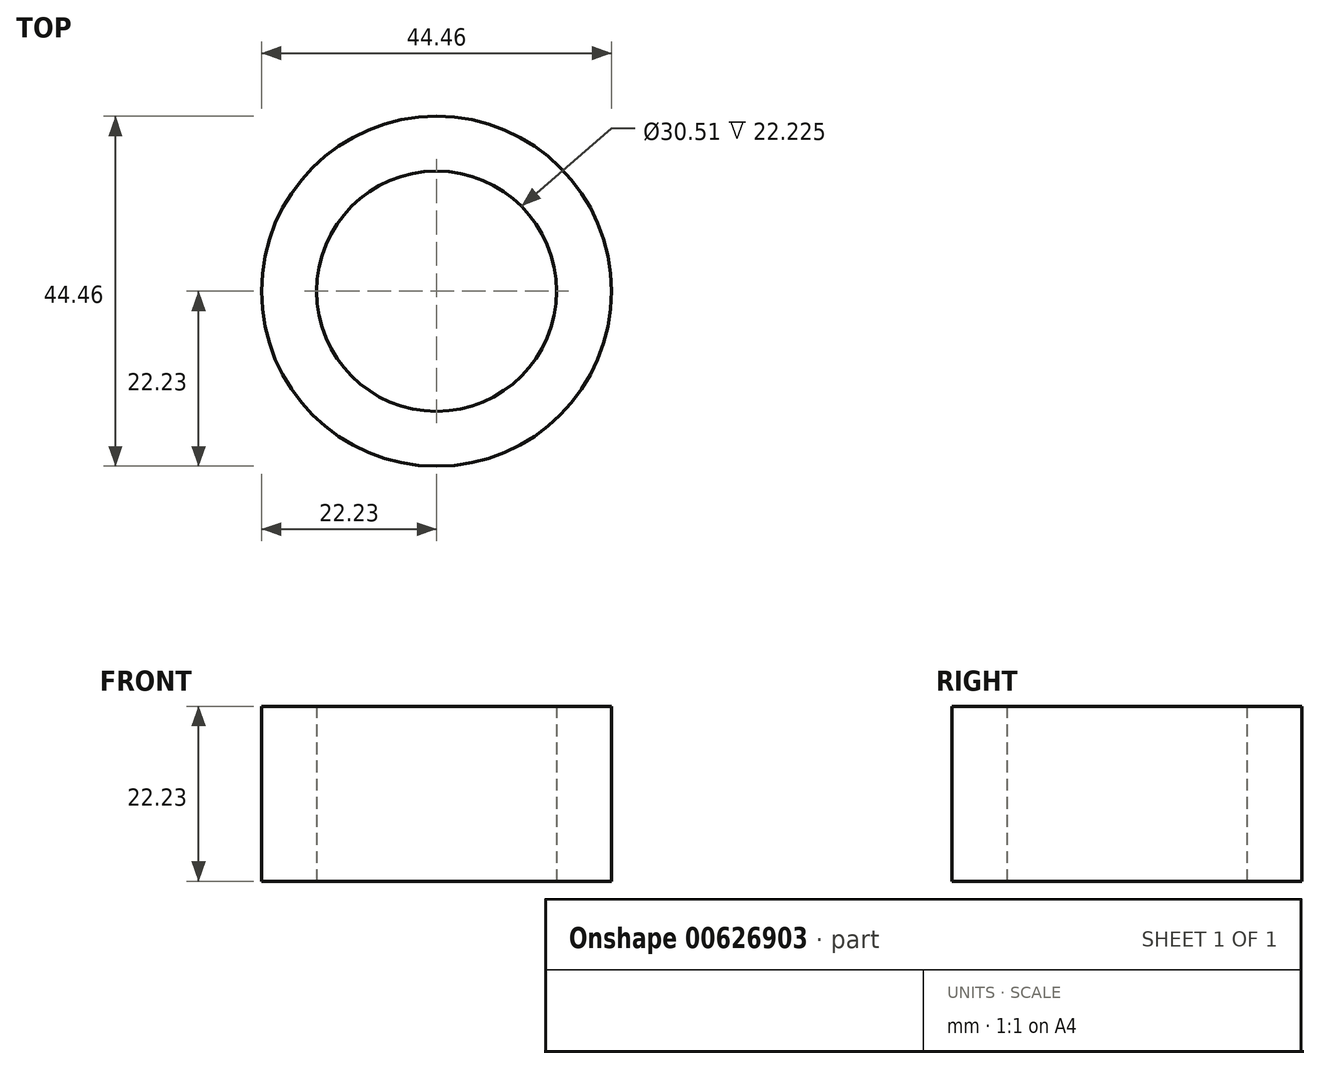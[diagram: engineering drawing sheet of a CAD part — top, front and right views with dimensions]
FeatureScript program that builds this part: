
annotation { "Feature Type Name" : "Feature", "Feature Type Description" : "" }
export const myFeature = defineFeature(function(context is Context, id is Id, definition is map)
    precondition{}
    {
        {
            var Q0;
            Q0=qCreatedBy(makeId("Top.planeOp"),FACE);
            var sketch = newSketch(context, id + "F0", { "sketchPlane" : qUnion([Q0])});
            skCircle(sketch, "E0", {"center": v(0, 0) * mm, "radius": 15.25 * mm});
            skCircle(sketch, "E1", {"center": v(0, 0) * mm, "radius": 22.23 * mm});
            skSolve(sketch);
        }
        {
            var Q0;
            Q0 = qSketchRegion(id + "F0", true);
            extrude(context, id + "F1", {"entities" : qUnion([Q0]), "depth" : 22.22 * mm, "offsetDistance" : 25.4 * mm});
        }
    });
